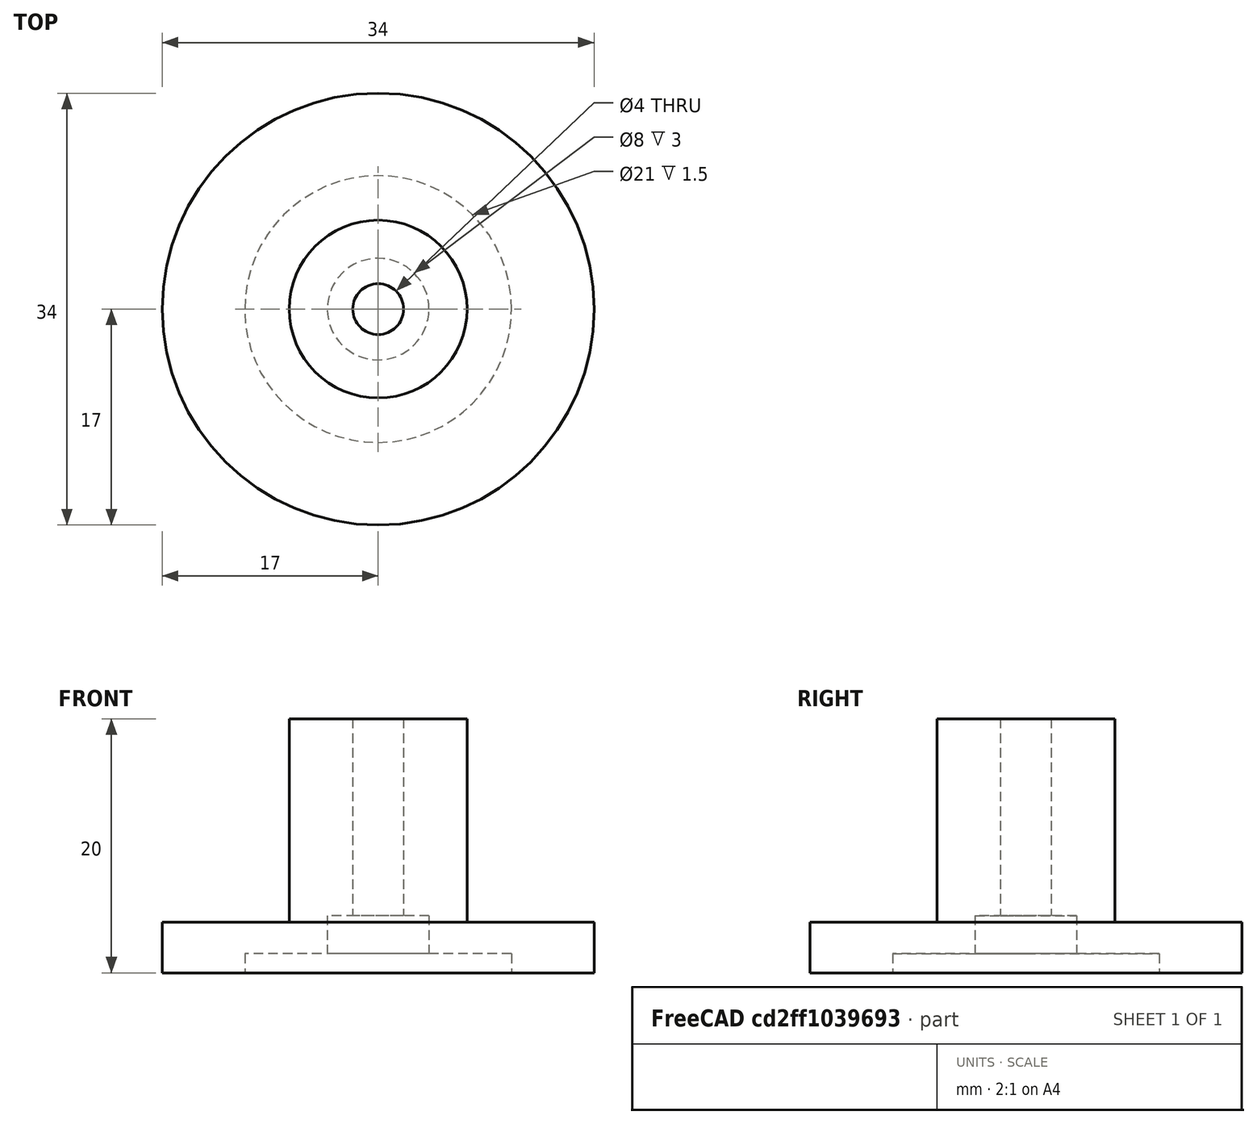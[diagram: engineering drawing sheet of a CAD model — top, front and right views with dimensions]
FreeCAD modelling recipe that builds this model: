
FCSTD DOCUMENT  (FreeCAD 0.19R20310 (Git))
Label: Bolzen
License: All rights reserved
LicenseURL: http://en.wikipedia.org/wiki/All_rights_reserved
objects: Sketcher::SketchObject×1, PartDesign::Revolution×1, PartDesign::Body×1
note: 4 computed .brp shape members not serialized (recipe doc carries the construction recipe); baked Part::Feature solids carry a one-line shape summary decoded from their .brp

FEATURE [Sketcher::SketchObject] Sketch
  MapMode = 5
  Placement = pos=(0,0,0) rot=(1,0,0;1.5708rad)
  Support = -> [XZ_Plane]
  sketch-geometry (10):
    g0: LineSegment StartX=2 StartY=20 StartZ=0 EndX=2 EndY=4.5 EndZ=0
    g1: LineSegment StartX=2 StartY=4.5 StartZ=0 EndX=4 EndY=4.5 EndZ=0
    g2: LineSegment StartX=4 StartY=4.5 StartZ=0 EndX=4 EndY=1.5 EndZ=0
    g3: LineSegment StartX=4 StartY=1.5 StartZ=0 EndX=10.5 EndY=1.5 EndZ=0
    g4: LineSegment StartX=10.5 StartY=1.5 StartZ=0 EndX=10.5 EndY=0 EndZ=0
    g5: LineSegment StartX=10.5 StartY=0 StartZ=0 EndX=17 EndY=0 EndZ=0
    g6: LineSegment StartX=17 StartY=0 StartZ=0 EndX=17 EndY=4 EndZ=0
    g7: LineSegment StartX=17 StartY=4 StartZ=0 EndX=7 EndY=4 EndZ=0
    g8: LineSegment StartX=7 StartY=4 StartZ=0 EndX=7 EndY=20 EndZ=0
    g9: LineSegment StartX=7 StartY=20 StartZ=0 EndX=2 EndY=20 EndZ=0
  constraints (30):
    c: Vertical(g0)
    c: Coincident(g0,g1)
    c: Horizontal(g1)
    c: Coincident(g1,g2)
    c: Coincident(g2,g3)
    c: Coincident(g3,g4)
    c: PointOnObject(g4,g-1)
    c: Coincident(g4,g5)
    c: Horizontal(g5)
    c: Coincident(g5,g6)
    c: Vertical(g6)
    c: Coincident(g6,g7)
    c: Horizontal(g7)
    c: Coincident(g7,g8)
    c: Vertical(g8)
    c: Coincident(g8,g9)
    c: Coincident(g9,g0)
    c: Horizontal(g9)
    c: Horizontal(g3)
    c: Vertical(g4)
    c: Vertical(g2)
    c: DistanceX(g-1,g0) = 2
    c: DistanceX(g-1,g8) = 7
    c: DistanceX(g-1,g2) = 4
    c: DistanceX(g-1,g4) = 10.5
    c: DistanceX(g-1,g5) = 17
    c: DistanceY(g2,g1) = 3
    c: DistanceY(g3,g7) = 2.5
    c: DistanceY(g4,g3) = 1.5
    c: DistanceY(g6,g8) = 16
FEATURE [PartDesign::Revolution] Revolution
  Angle = 360
  Axis = (0,2e-16,1)
  Base = (0,0,0)
  Placement = pos=(0,0,0) rot=(1,0,0;1.5708rad)
  Profile = -> Sketch
  ReferenceAxis = -> Sketch [V_Axis]
FEATURE [PartDesign::Body] Body
  Group = -> [Sketch,Revolution]
  Origin = -> Origin
  Tip = -> Revolution
